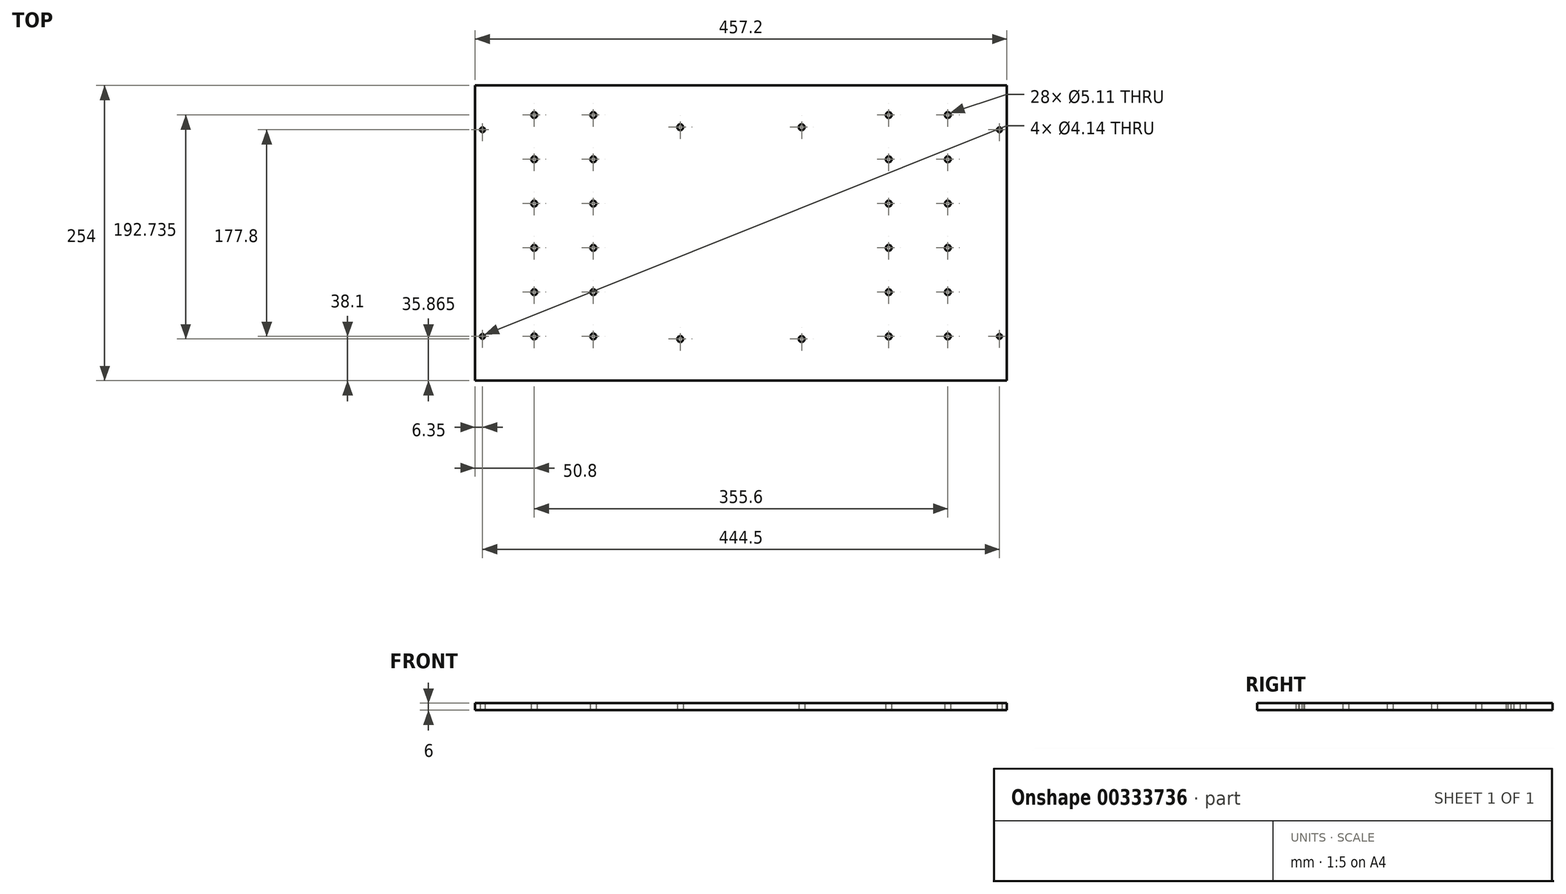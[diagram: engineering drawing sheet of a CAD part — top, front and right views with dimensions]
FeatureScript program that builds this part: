
annotation { "Feature Type Name" : "Feature", "Feature Type Description" : "" }
export const myFeature = defineFeature(function(context is Context, id is Id, definition is map)
    precondition{}
    {
        {
            var Q0;
            Q0=qCreatedBy(makeId("Top.planeOp"),FACE);
            var sketch = newSketch(context, id + "F0", { "sketchPlane" : qUnion([Q0])});
            skLineSegment(sketch, "E0.bottom", {"start": v(228.6, 127) * mm, "end": v(-228.6, 127) * mm});
            skLineSegment(sketch, "E0.top", {"start": v(228.6, -127) * mm, "end": v(-228.6, -127) * mm});
            skLineSegment(sketch, "E0.left", {"start": v(228.6, 127) * mm, "end": v(228.6, -127) * mm});
            skLineSegment(sketch, "E0.right", {"start": v(-228.6, 127) * mm, "end": v(-228.6, -127) * mm});
            skPoint(sketch, "E0.middle", {"position": v(0, 0) * mm});
            skLineSegment(sketch, "E1", {"start": v(-177.8, 127) * mm, "end": v(-177.8, -127) * mm, "construction": true});
            skLineSegment(sketch, "E2", {"start": v(-127, -127) * mm, "end": v(-127, 127) * mm, "construction": true});
            skLineSegment(sketch, "E3", {"start": v(127, 127) * mm, "end": v(127, -127) * mm, "construction": true});
            skLineSegment(sketch, "E4", {"start": v(177.8, -127) * mm, "end": v(177.8, 127) * mm, "construction": true});
            skLineSegment(sketch, "E5", {"start": v(-152.4, 127) * mm, "end": v(-152.4, -127) * mm, "construction": true});
            skLineSegment(sketch, "E6", {"start": v(152.4, 127) * mm, "end": v(152.4, -127) * mm, "construction": true});
            skLineSegment(sketch, "E7", {"start": v(-177.8, 0) * mm, "end": v(-127, 0) * mm, "construction": true});
            skPoint(sketch, "E8", {"position": v(-152.4, 0) * mm});
            skLineSegment(sketch, "E9", {"start": v(127, 0) * mm, "end": v(177.8, 0) * mm, "construction": true});
            skPoint(sketch, "E10", {"position": v(152.4, 0) * mm});
            skCircle(sketch, "E11", {"center": v(-177.8, 101.6) * mm, "radius": 2.55 * mm});
            skCircle(sketch, "E12.0.1.0", {"center": v(-177.8, 63.5) * mm, "radius": 2.55 * mm});
            skCircle(sketch, "E12.0.2.0", {"center": v(-177.8, 25.4) * mm, "radius": 2.55 * mm});
            skCircle(sketch, "E12.0.3.0", {"center": v(-177.8, -12.7) * mm, "radius": 2.55 * mm});
            skCircle(sketch, "E12.0.4.0", {"center": v(-177.8, -50.8) * mm, "radius": 2.55 * mm});
            skCircle(sketch, "E12.0.5.0", {"center": v(-177.8, -88.9) * mm, "radius": 2.55 * mm});
            skCircle(sketch, "E12.1.0.0", {"center": v(-127, 101.6) * mm, "radius": 2.55 * mm});
            skCircle(sketch, "E12.1.1.0", {"center": v(-127, 63.5) * mm, "radius": 2.55 * mm});
            skCircle(sketch, "E12.1.2.0", {"center": v(-127, 25.4) * mm, "radius": 2.55 * mm});
            skCircle(sketch, "E12.1.3.0", {"center": v(-127, -12.7) * mm, "radius": 2.55 * mm});
            skCircle(sketch, "E12.1.4.0", {"center": v(-127, -50.8) * mm, "radius": 2.55 * mm});
            skCircle(sketch, "E12.1.5.0", {"center": v(-127, -88.9) * mm, "radius": 2.55 * mm});
            skLineSegment(sketch, "E12.direction1", {"start": v(-177.8, 101.6) * mm, "end": v(-127, 101.6) * mm, "construction": true});
            skLineSegment(sketch, "E12.direction2", {"start": v(-177.8, 101.6) * mm, "end": v(-177.8, 63.5) * mm, "construction": true});
            skCircle(sketch, "E13", {"center": v(127, 101.6) * mm, "radius": 2.55 * mm});
            skCircle(sketch, "E14.0.1.0", {"center": v(127, 63.5) * mm, "radius": 2.55 * mm});
            skCircle(sketch, "E14.0.2.0", {"center": v(127, 25.4) * mm, "radius": 2.55 * mm});
            skCircle(sketch, "E14.0.3.0", {"center": v(127, -12.7) * mm, "radius": 2.55 * mm});
            skCircle(sketch, "E14.0.4.0", {"center": v(127, -50.8) * mm, "radius": 2.55 * mm});
            skCircle(sketch, "E14.0.5.0", {"center": v(127, -88.9) * mm, "radius": 2.55 * mm});
            skCircle(sketch, "E14.1.0.0", {"center": v(177.8, 101.6) * mm, "radius": 2.55 * mm});
            skCircle(sketch, "E14.1.1.0", {"center": v(177.8, 63.5) * mm, "radius": 2.55 * mm});
            skCircle(sketch, "E14.1.2.0", {"center": v(177.8, 25.4) * mm, "radius": 2.55 * mm});
            skCircle(sketch, "E14.1.3.0", {"center": v(177.8, -12.7) * mm, "radius": 2.55 * mm});
            skCircle(sketch, "E14.1.4.0", {"center": v(177.8, -50.8) * mm, "radius": 2.55 * mm});
            skCircle(sketch, "E14.1.5.0", {"center": v(177.8, -88.9) * mm, "radius": 2.55 * mm});
            skLineSegment(sketch, "E14.direction1", {"start": v(127, 101.6) * mm, "end": v(177.8, 101.6) * mm, "construction": true});
            skLineSegment(sketch, "E14.direction2", {"start": v(127, 101.6) * mm, "end": v(127, 63.5) * mm, "construction": true});
            skLineSegment(sketch, "E15.bottom", {"start": v(57.4, -96.34) * mm, "end": v(-57.4, -96.34) * mm, "construction": true});
            skLineSegment(sketch, "E15.top", {"start": v(57.4, 96.34) * mm, "end": v(-57.4, 96.34) * mm, "construction": true});
            skLineSegment(sketch, "E15.left", {"start": v(57.4, -96.34) * mm, "end": v(57.4, 96.34) * mm, "construction": true});
            skLineSegment(sketch, "E15.right", {"start": v(-57.4, -96.34) * mm, "end": v(-57.4, 96.34) * mm, "construction": true});
            skLineSegment(sketch, "E16.bottom", {"start": v(52.2, -91.14) * mm, "end": v(-52.2, -91.14) * mm, "construction": true});
            skLineSegment(sketch, "E16.top", {"start": v(52.2, 91.14) * mm, "end": v(-52.2, 91.14) * mm, "construction": true});
            skLineSegment(sketch, "E16.left", {"start": v(52.2, -91.14) * mm, "end": v(52.2, 91.14) * mm, "construction": true});
            skLineSegment(sketch, "E16.right", {"start": v(-52.2, -91.14) * mm, "end": v(-52.2, 91.14) * mm, "construction": true});
            skCircle(sketch, "E17", {"center": v(-52.2, 91.14) * mm, "radius": 2.55 * mm});
            skCircle(sketch, "E18", {"center": v(52.2, 91.14) * mm, "radius": 2.55 * mm});
            skCircle(sketch, "E19", {"center": v(52.2, -91.14) * mm, "radius": 2.55 * mm});
            skCircle(sketch, "E20", {"center": v(-52.2, -91.14) * mm, "radius": 2.55 * mm});
            skLineSegment(sketch, "E21.bottom", {"start": v(-222.25, -88.9) * mm, "end": v(222.25, -88.9) * mm, "construction": true});
            skLineSegment(sketch, "E21.top", {"start": v(-222.25, 88.9) * mm, "end": v(222.25, 88.9) * mm, "construction": true});
            skLineSegment(sketch, "E21.left", {"start": v(-222.25, -88.9) * mm, "end": v(-222.25, 88.9) * mm, "construction": true});
            skLineSegment(sketch, "E21.right", {"start": v(222.25, -88.9) * mm, "end": v(222.25, 88.9) * mm, "construction": true});
            skCircle(sketch, "E22", {"center": v(-222.25, 88.9) * mm, "radius": 2.07 * mm});
            skCircle(sketch, "E23", {"center": v(-222.25, -88.9) * mm, "radius": 2.07 * mm});
            skCircle(sketch, "E24", {"center": v(222.25, -88.9) * mm, "radius": 2.07 * mm});
            skCircle(sketch, "E25", {"center": v(222.25, 88.9) * mm, "radius": 2.07 * mm});
            skSolve(sketch);
        }
        {
            var Q0;
            Q0 = qSketchRegion(id + "F0", true);
            extrude(context, id + "F1", {"entities" : qUnion([Q0]), "depth" : 6 * mm});
        }
    });
